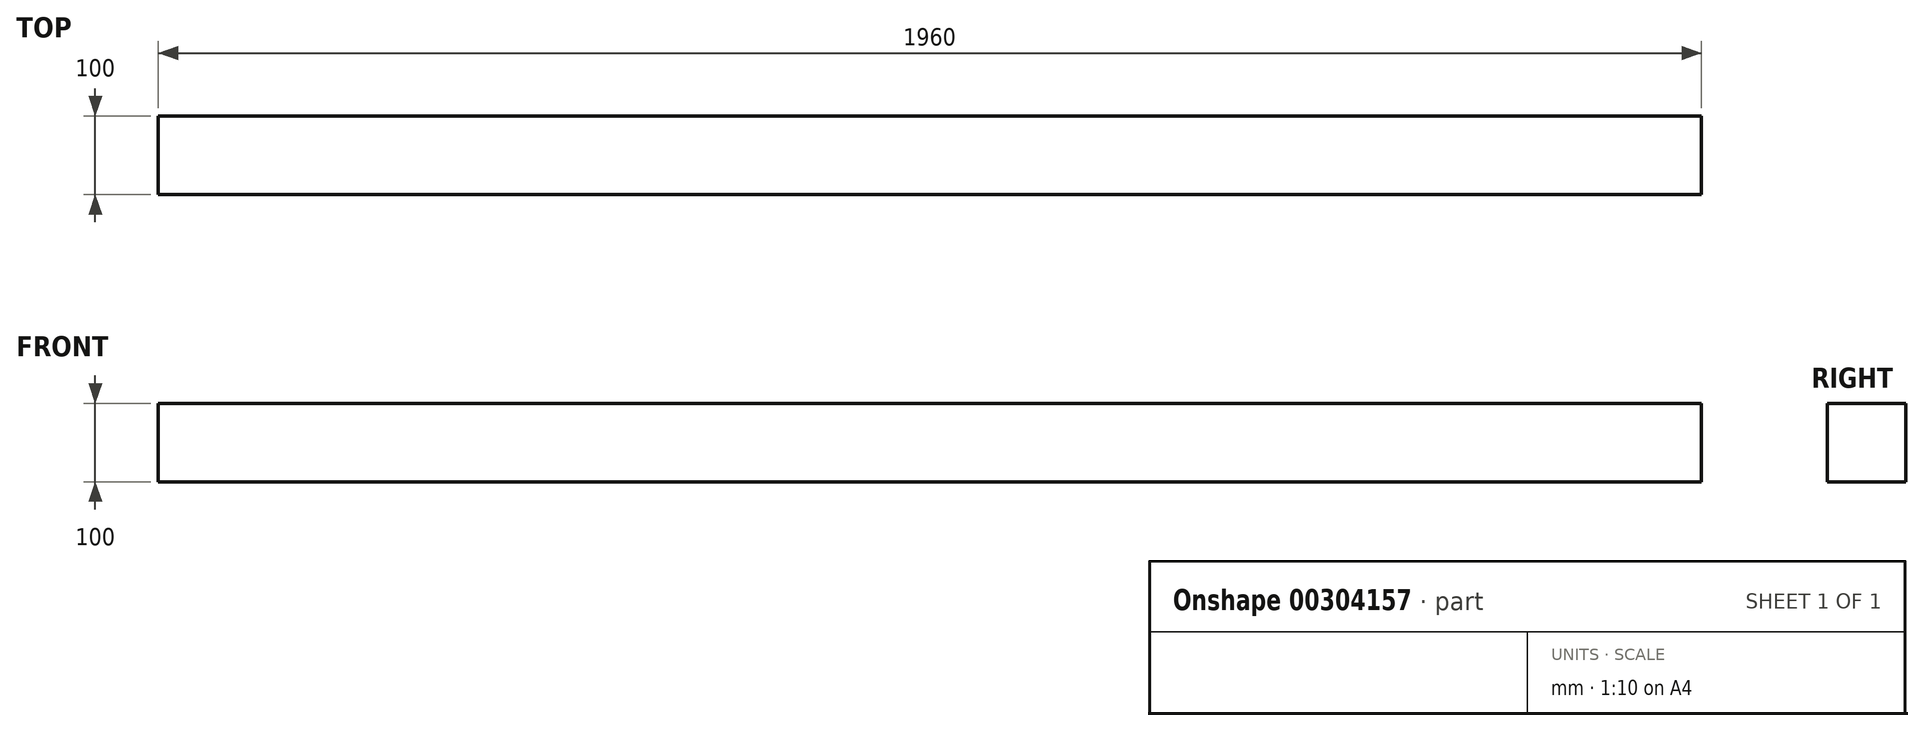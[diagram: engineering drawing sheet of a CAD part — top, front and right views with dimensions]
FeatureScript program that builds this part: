
annotation { "Feature Type Name" : "Feature", "Feature Type Description" : "" }
export const myFeature = defineFeature(function(context is Context, id is Id, definition is map)
    precondition{}
    {
        {
            var Q0;
            Q0=qCreatedBy(makeId("Top.planeOp"),FACE);
            var sketch = newSketch(context, id + "F0", { "sketchPlane" : qUnion([Q0])});
            skLineSegment(sketch, "E0.bottom", {"start": v(-977.73, -262.81) * mm, "end": v(982.27, -262.81) * mm});
            skLineSegment(sketch, "E0.top", {"start": v(-977.73, -362.81) * mm, "end": v(982.27, -362.81) * mm});
            skLineSegment(sketch, "E0.left", {"start": v(-977.73, -262.81) * mm, "end": v(-977.73, -362.81) * mm});
            skLineSegment(sketch, "E0.right", {"start": v(982.27, -262.81) * mm, "end": v(982.27, -362.81) * mm});
            skSolve(sketch);
        }
        {
            var Q0;
            Q0=makeQuery(id+"F0.imprint","IMPRINT",FACE,{"disambiguationData":[TD([[makeQuery(id+"F0.imprint","IMPRINT",EDGE,{"derivedFrom":sQuery(id+"F0.wireOp",EDGE,"E0.bottom")}),-1.0]])]});
            extrude(context, id + "F1", {"entities" : qUnion([Q0]), "depth" : 100 * mm});
        }
    });
